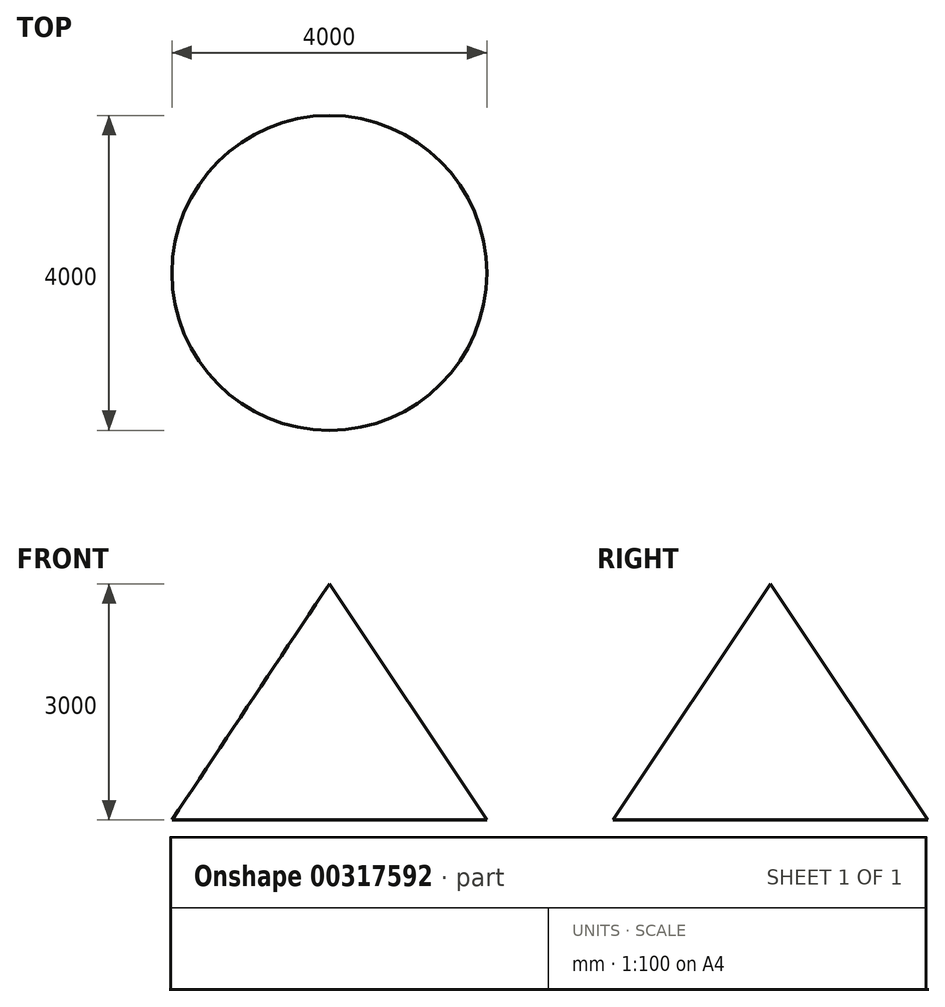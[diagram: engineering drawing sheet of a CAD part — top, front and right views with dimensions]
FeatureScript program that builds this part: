
annotation { "Feature Type Name" : "Feature", "Feature Type Description" : "" }
export const myFeature = defineFeature(function(context is Context, id is Id, definition is map)
    precondition{}
    {
        {
            var Q0;
            Q0=qCreatedBy(makeId("Front.planeOp"),FACE);
            var sketch = newSketch(context, id + "F0", { "sketchPlane" : qUnion([Q0])});
            skLineSegment(sketch, "E0", {"start": v(0, 0) * mm, "end": v(2000, 0) * mm});
            skLineSegment(sketch, "E1", {"start": v(0, 0) * mm, "end": v(0, 3000) * mm});
            skLineSegment(sketch, "E2", {"start": v(0, 3000) * mm, "end": v(2000, 0) * mm});
            skSolve(sketch);
        }
        {
            var Q0;
            Q0=makeQuery(id+"F0.imprint","IMPRINT",FACE,{"disambiguationData":[TD([[makeQuery(id+"F0.imprint","IMPRINT",EDGE,{"derivedFrom":sQuery(id+"F0.wireOp",EDGE,"E0")}),1.0]])]});
            var Q1;
            Q1=sQuery(id+"F0.wireOp",EDGE,"E1");
            revolve(context, id + "F1", {"entities" : qUnion([Q0]), "axis" : qUnion([Q1]), "revolveType" : RevolveType.FULL});
        }
    });
